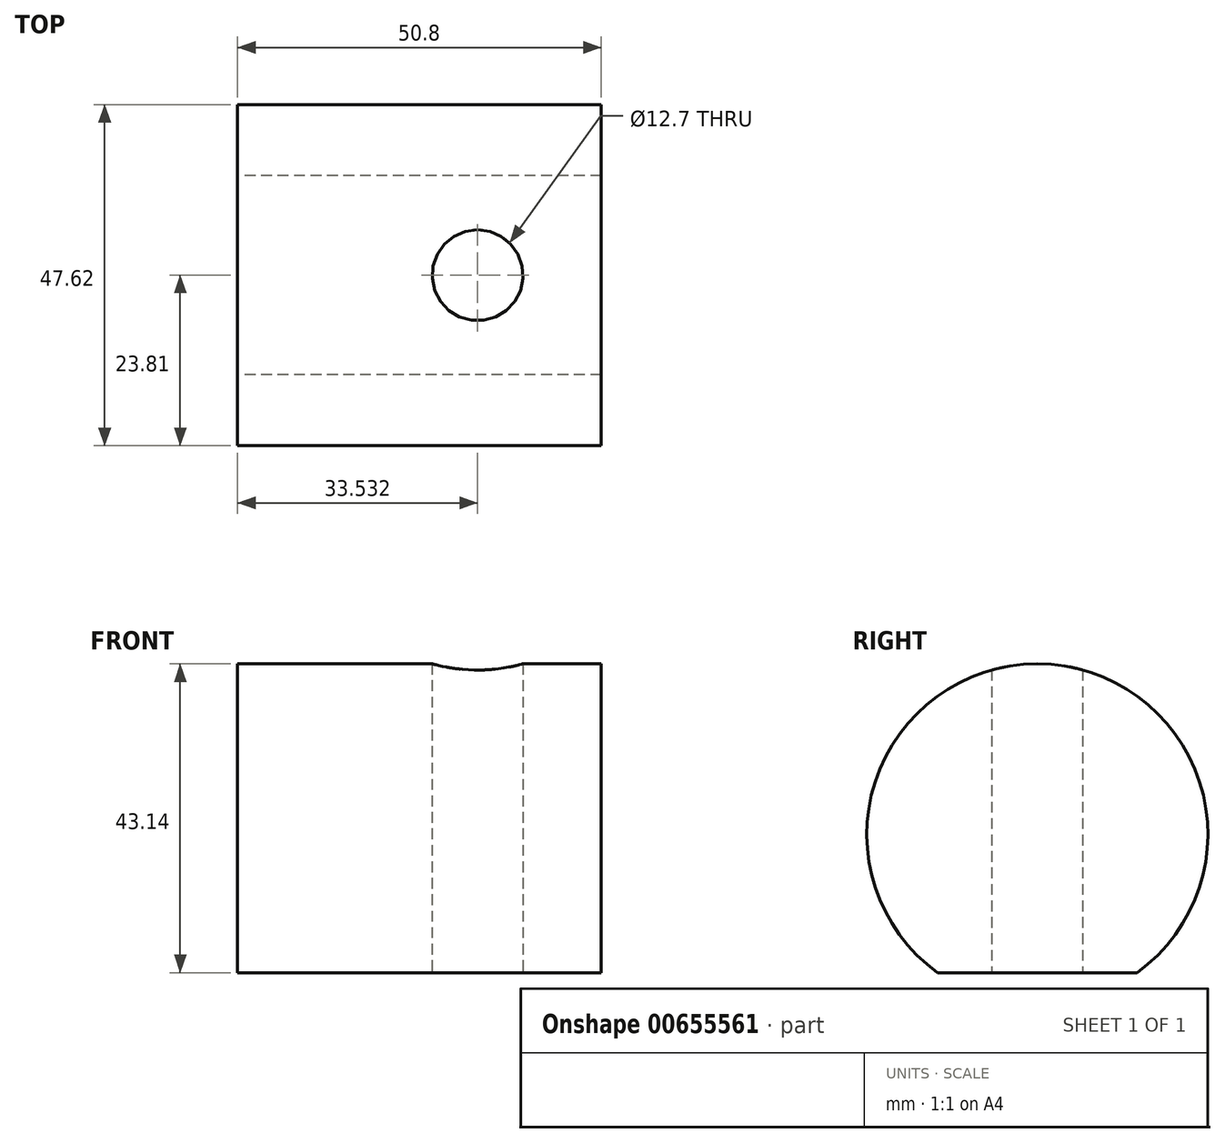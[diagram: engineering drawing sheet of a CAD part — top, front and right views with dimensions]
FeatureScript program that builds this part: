
annotation { "Feature Type Name" : "Feature", "Feature Type Description" : "" }
export const myFeature = defineFeature(function(context is Context, id is Id, definition is map)
    precondition{}
    {
        {
            var Q0;
            Q0=qCreatedBy(makeId("Right.planeOp"),FACE);
            var sketch = newSketch(context, id + "F0", { "sketchPlane" : qUnion([Q0])});
            skArc(sketch, "E0", {"start": v(13.92, -1.65) * mm, "mid": v(0, 41.5) * mm, "end": v(-13.92, -1.65) * mm});
            skLineSegment(sketch, "E1", {"start": v(13.92, -1.65) * mm, "end": v(-13.92, -1.65) * mm});
            skPoint(sketch, "E2.start.orphan", {"position": v(-15.95, 0) * mm});
            skSolve(sketch);
        }
        {
            var Q0;
            Q0=makeQuery(id+"F0.imprint","IMPRINT",FACE,{"disambiguationData":[TD([[makeQuery(id+"F0.imprint","IMPRINT",EDGE,{"derivedFrom":sQuery(id+"F0.wireOp",EDGE,"E0")}),1.0]])]});
            extrude(context, id + "F1", {"entities" : qUnion([Q0]), "depth" : 50.8 * mm, "offsetDistance" : 25.4 * mm});
        }
        {
            var Q0;
            Q0=makeQuery(id+"F1.opExtrude","SWEPT_FACE",FACE,{"disambiguationData":[OSD([sQuery(id+"F0.wireOp",EDGE,"E1")])]});
            var sketch = newSketch(context, id + "F2", { "sketchPlane" : qUnion([Q0])});
            skCircle(sketch, "E3", {"center": v(33.53, 0) * mm, "radius": 6.35 * mm});
            skSolve(sketch);
        }
        {
            var Q0;
            Q0=sQuery(id+"F2.wireOp",VERTEX,"E3.center");
            var Q1;
            Q1=makeQuery(id+"F1.opExtrude","SWEPT_BODY",BODY,{"disambiguationData":[OSD([sQuery(id+"F0.wireOp",EDGE,"E0"),sQuery(id+"F0.wireOp",EDGE,"E1")])]});
            hole(context, id + "F3", {"style" : HoleStyle.SIMPLE, "endStyle" : HoleEndStyle.BLIND, "holeDiameter" : 12.7 * mm, "majorDiameter" : 6.35 * mm, "holeDepth" : 50.8 * mm, "isTappedThrough" : true, "tappedDepth" : 12.7 * mm, "tapClearance" : 3, "startFromSketch" : true, "locations" : qUnion([Q0]), "scope" : qUnion([Q1])});
        }
    });
